# Revit family: Zumtobel TECTON MPO LED
name_source: partatom
category: Lighting Fixtures
revit_build: Autodesk Revit 2014 (Build: 20140709_2115(x64)
units: mm (PartAtom-declared; Revit-internal decimal feet)

## types (1)
- TECTON MPO LED5500-840 L1500
    Apparent Load = 41 VA
    Body = Zumtobel_Metal_White
    Color Filter = 16777215
    Cover = Zumtobel_Lamp_Self_llumination_Opaque
    Default Elevation = 0 mm  [stored 0 ft]
    Description = Single luminaire
    Dimming Lamp Color Temperature Shift = <None>
    Emit Shape Visible in Rendering = No
    Emit from Rectangle Length = 98 mm  [stored 0.321522 ft]
    Emit from Rectangle Width = 1516 mm  [stored 4.97375 ft]
    Lamp = LED
    Length = 1522 mm  [stored 4.99344 ft]
    Manufacturer = Zumtobel Ligthing
    Model = 42184102
    Photometric Web File = 42184102_(STD_LEO).IES
    Tilt Angle = 90.00°
    URL = http://www.zumtobel.com
    Voltage = 230 V
    Wattage Comments = 230
    Width = 97 mm  [stored 0.318241 ft]

note: [stored X ft] marks values corroborated as IEEE doubles in the binary element streams (Revit-internal decimal feet)

## geometry (parser evidence)
native form markers: Blend x8, Sweep x2
no freeform markers — native parametric forms only
